# Revit family: F-LINE-R1X115-30xxx
name_source: partatom
category: Oprawy oświetleniowe
units: mm (PartAtom-declared; Revit-internal decimal feet)

## family parameters
Numer OmniClass = 23.80.70.11
Obiekt nadrzędny = Powierzchnia
Punkt obliczania pomieszczeń = Nie
Tnij formami wycięć po wczytaniu = Nie
Typ części = Normalny
Tytuł OmniClass = Luminaries for Internal Lighting
Współdzielony = Nie
Wymiar okrągłego złącza = Użyj średnicy
Źródło światła = Tak

## types (6) — shared parameters
Emituj kształt widoczny w renderingu = Nie
Emituj z długości prostokąta = 50 mm  [stored 0.164042 ft]
Emituj z szerokości prostokąta = 1155 mm  [stored 3.78937 ft]
Filtr koloru = 16777215
Kod zespołu = D5020200
Lampa = LED
Obciążenie pozorne = 35 VA
Odchylenie kierunku = 90.00°
Producent = RIDI Leuchten GmbH
URL = www.ridi.de
Zmiana temperatury barwowej przyciemniania lampy = <Brak>
brand = RIDI
conformity mark = CE
electrical safety class = 1
height = 45 mm  [stored 0.147638 ft]
ingress protection (IP) code = IP20
length = 1253 mm  [stored 4.11089 ft]
nominal frequency = 50-60Hz
nominal voltage = 230
rated input power = 35
voltage type (AC, DC, UC) = AC
width = 150 mm
zero-valued in all types: Domyślna rzędna

## per-type parameters (varying)
| type | Model | Plik sieci fotometrycznej | weight |
| F-LINE-R1X115/30ND-SM | 0650210 | F-LINE-R1x11530DA-SM.IES | 3,53 |
| F-LINE-R1X115/30DA-SM | 0660210 | F-LINE-R1x11530DA-SM.IES | 3.3 |
| F-LINE-R1X115/30ND-O | 0650240 | F-LINE-R1x11530DA-O.IES | 3.7 |
| F-LINE-R1X115/30DA-O | 0660240 | F-LINE-R1x11530DA-O.IES | 3.7 |
| F-LINE-R1X115/30ND-MPS | 0650241 | F-LINE-R1x11530DA-MPS.IES | 3.7 |
| F-LINE-R1X115/30DA-MPS | 0660241 | F-LINE-R1x11530DA-MPS.IES | 3.7 |

note: column(s) folded — value = type name in every type: product name

note: [stored X ft] marks values corroborated as IEEE doubles in the binary element streams (Revit-internal decimal feet)
